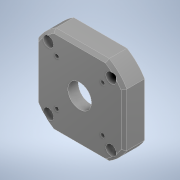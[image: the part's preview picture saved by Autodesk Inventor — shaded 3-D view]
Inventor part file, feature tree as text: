
AUTODESK INVENTOR PART (.ipt)
format: ipt  version: 2022 (Build 260153000, 153)  size: 184,832 bytes
history: mixed  units: in
note: dims shown in document units (in); Inventor stores cm internally (conversion verified against a paired STEP export)
features: extrude x3, sketch x3, chamfer x1, imported_body x1
ambient origin geometry x8: Origin, YZ Plane, XZ Plane, XY Plane, X Axis, Y Axis, Z Axis, Center Point
bodies: Solid1 (imported_parasolid)
feature tree (8):
  extrude  "Extrusion1"  Depth=0.3937in TaperAngle=0.0deg
  extrude  "Extrusion2"  Depth=0.3937in TaperAngle=0.0deg
  extrude  "Extrusion3"  TaperAngle=0.0deg  [1 undecoded]
  sketch  "Sketch1"  dims[d0=0.1102in d1=0.3937in d2=0.0in]
  sketch  "Sketch2"  dims[d3=0.5906in d4=0.3937in d5=0.0in]
  sketch  "Sketch3"  dims[d6=0.6299in d7=0.0in d8=0.0in]
  chamfer  "Chamfer2"  [1 undecoded]
  imported_body  NMx_Import_Brep_tag  [imported B-rep: ~32 faces, bbox_mm=[53.213203, 60.0, 14.0]]
note: 2 required parameter values undecoded (feature->parameter linkage not recoverable at this tier; creation-order binding heuristic only, values carry confidence <= 0.55)
